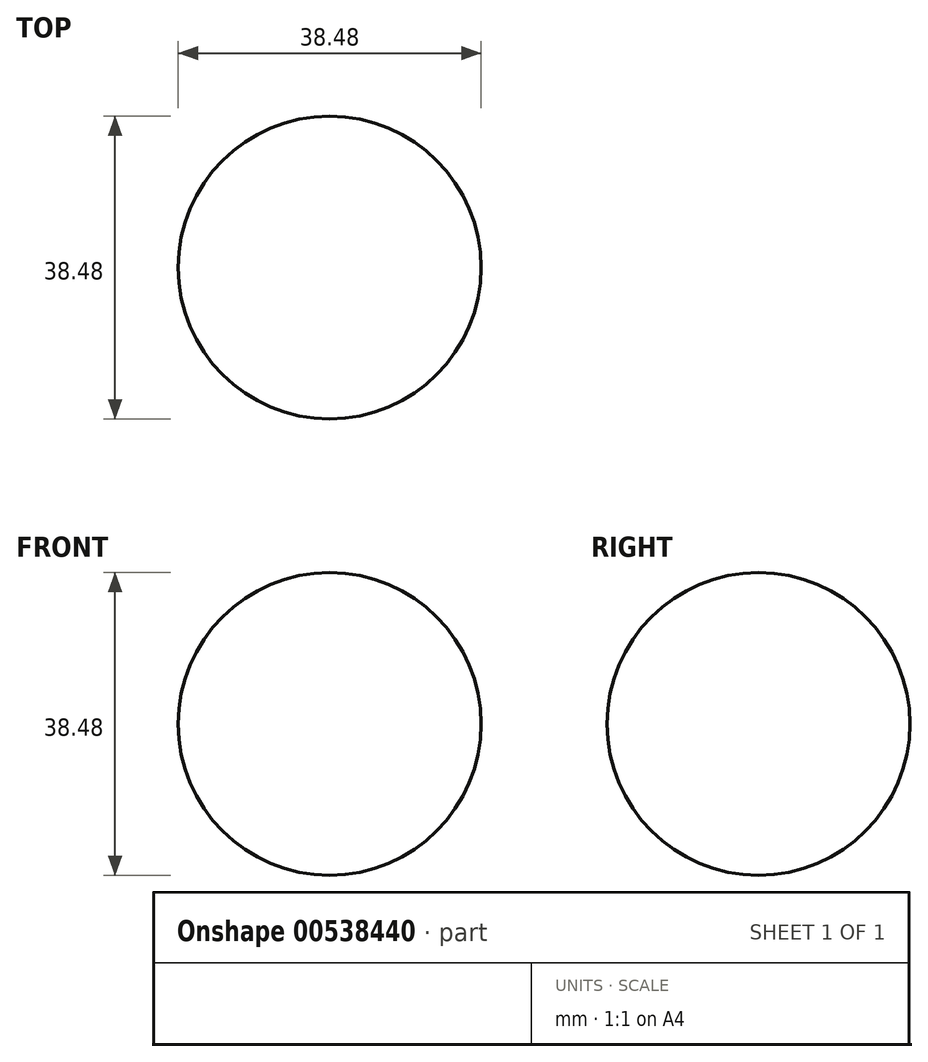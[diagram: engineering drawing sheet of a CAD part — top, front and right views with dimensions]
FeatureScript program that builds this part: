
annotation { "Feature Type Name" : "Feature", "Feature Type Description" : "" }
export const myFeature = defineFeature(function(context is Context, id is Id, definition is map)
    precondition{}
    {
        {
            var Q0;
            Q0=qCreatedBy(makeId("Front.planeOp"),FACE);
            var sketch = newSketch(context, id + "F0", { "sketchPlane" : qUnion([Q0])});
            skArc(sketch, "E0", {"start": v(0, 19.24) * mm, "mid": v(-13.6, 13.6) * mm, "end": v(-19.24, 0) * mm});
            skArc(sketch, "E1", {"start": v(0, 19.24) * mm, "mid": v(13.6, 13.6) * mm, "end": v(19.24, 0) * mm});
            skLineSegment(sketch, "E2", {"start": v(-19.24, 0) * mm, "end": v(19.24, 0) * mm});
            skSolve(sketch);
        }
        {
            var Q0;
            Q0=makeQuery(id+"F0.imprint","IMPRINT",FACE,{"disambiguationData":[TD([[makeQuery(id+"F0.imprint","IMPRINT",EDGE,{"derivedFrom":sQuery(id+"F0.wireOp",EDGE,"E0")}),1.0]])]});
            var Q1;
            Q1=sQuery(id+"F0.wireOp",EDGE,"E2");
            revolve(context, id + "F1", {"entities" : qUnion([Q0]), "axis" : qUnion([Q1]), "revolveType" : RevolveType.FULL});
        }
    });
